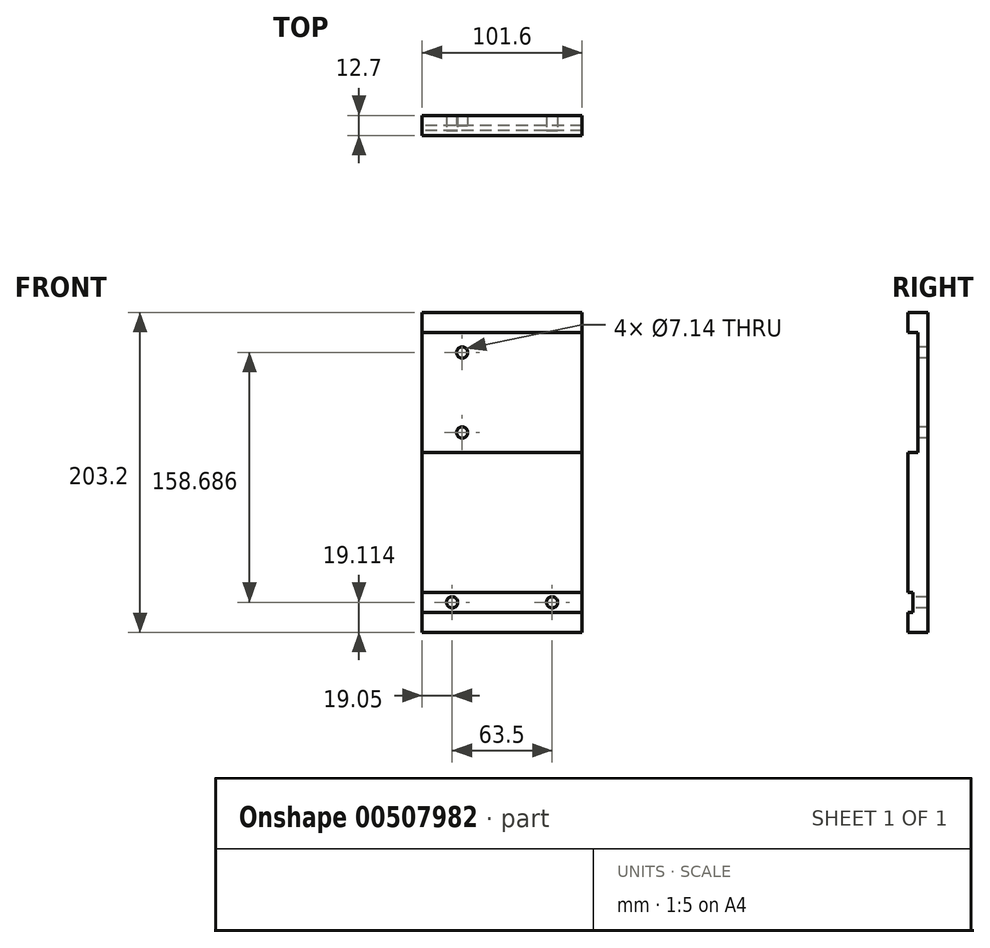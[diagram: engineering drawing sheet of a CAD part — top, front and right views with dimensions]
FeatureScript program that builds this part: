
annotation { "Feature Type Name" : "Feature", "Feature Type Description" : "" }
export const myFeature = defineFeature(function(context is Context, id is Id, definition is map)
    precondition{}
    {
        {
            var Q0;
            Q0=qCreatedBy(makeId("Right.planeOp"),FACE);
            var sketch = newSketch(context, id + "F0", { "sketchPlane" : qUnion([Q0])});
            skLineSegment(sketch, "E0", {"start": v(14.03, 136.3) * mm, "end": v(14.03, -66.9) * mm});
            skLineSegment(sketch, "E1", {"start": v(14.03, -66.9) * mm, "end": v(1.33, -66.9) * mm});
            skLineSegment(sketch, "E2", {"start": v(4.5, -41.37) * mm, "end": v(1.33, -41.37) * mm});
            skLineSegment(sketch, "E3", {"start": v(1.33, -41.37) * mm, "end": v(1.33, 47.4) * mm});
            skLineSegment(sketch, "E4", {"start": v(1.33, 47.4) * mm, "end": v(7.68, 47.4) * mm});
            skLineSegment(sketch, "E5", {"start": v(7.68, 47.4) * mm, "end": v(7.68, 123.6) * mm});
            skLineSegment(sketch, "E6", {"start": v(7.68, 123.6) * mm, "end": v(1.33, 123.6) * mm});
            skLineSegment(sketch, "E7", {"start": v(1.33, 123.6) * mm, "end": v(1.33, 136.3) * mm});
            skLineSegment(sketch, "E8", {"start": v(1.33, 136.3) * mm, "end": v(14.03, 136.3) * mm});
            skLineSegment(sketch, "E9", {"start": v(4.5, -41.37) * mm, "end": v(4.5, -54.2) * mm});
            skLineSegment(sketch, "E10", {"start": v(4.5, -54.2) * mm, "end": v(1.33, -54.2) * mm});
            skLineSegment(sketch, "E11", {"start": v(1.33, -54.2) * mm, "end": v(1.33, -66.9) * mm});
            skSolve(sketch);
        }
        {
            var Q0;
            Q0 = qSketchRegion(id + "F0", true);
            extrude(context, id + "F1", {"entities" : qUnion([Q0]), "depth" : 101.6 * mm});
        }
        {
            var Q0;
            Q0=makeQuery(id+"F1.opExtrude","SWEPT_FACE",FACE,{"disambiguationData":[OSD([sQuery(id+"F0.wireOp",EDGE,"E9")])]});
            var sketch = newSketch(context, id + "F2", { "sketchPlane" : qUnion([Q0])});
            skCircle(sketch, "E12", {"center": v(19.05, -47.79) * mm, "radius": 3.57 * mm});
            skCircle(sketch, "E13", {"center": v(82.55, -47.79) * mm, "radius": 3.57 * mm});
            skSolve(sketch);
        }
        {
            var Q0;
            Q0 = qSketchRegion(id + "F2", true);
            extrude(context, id + "F3", {"entities" : qUnion([Q0]), "operationType" : NewBodyOperationType.REMOVE, "endBound" : BoundingType.UP_TO_NEXT, "oppositeDirection" : true, "depth" : 25.4 * mm});
        }
        {
            var Q0;
            Q0=makeQuery(id+"F1.opExtrude","SWEPT_FACE",FACE,{"disambiguationData":[OSD([sQuery(id+"F0.wireOp",EDGE,"E5")])]});
            var sketch = newSketch(context, id + "F4", { "sketchPlane" : qUnion([Q0])});
            skCircle(sketch, "E14", {"center": v(25.4, 110.9) * mm, "radius": 3.57 * mm});
            skCircle(sketch, "E15", {"center": v(25.4, 60.1) * mm, "radius": 3.57 * mm});
            skSolve(sketch);
        }
        {
            var Q0;
            Q0 = qSketchRegion(id + "F4", true);
            extrude(context, id + "F5", {"entities" : qUnion([Q0]), "operationType" : NewBodyOperationType.REMOVE, "endBound" : BoundingType.UP_TO_NEXT, "oppositeDirection" : true, "depth" : 25.4 * mm});
        }
    });
